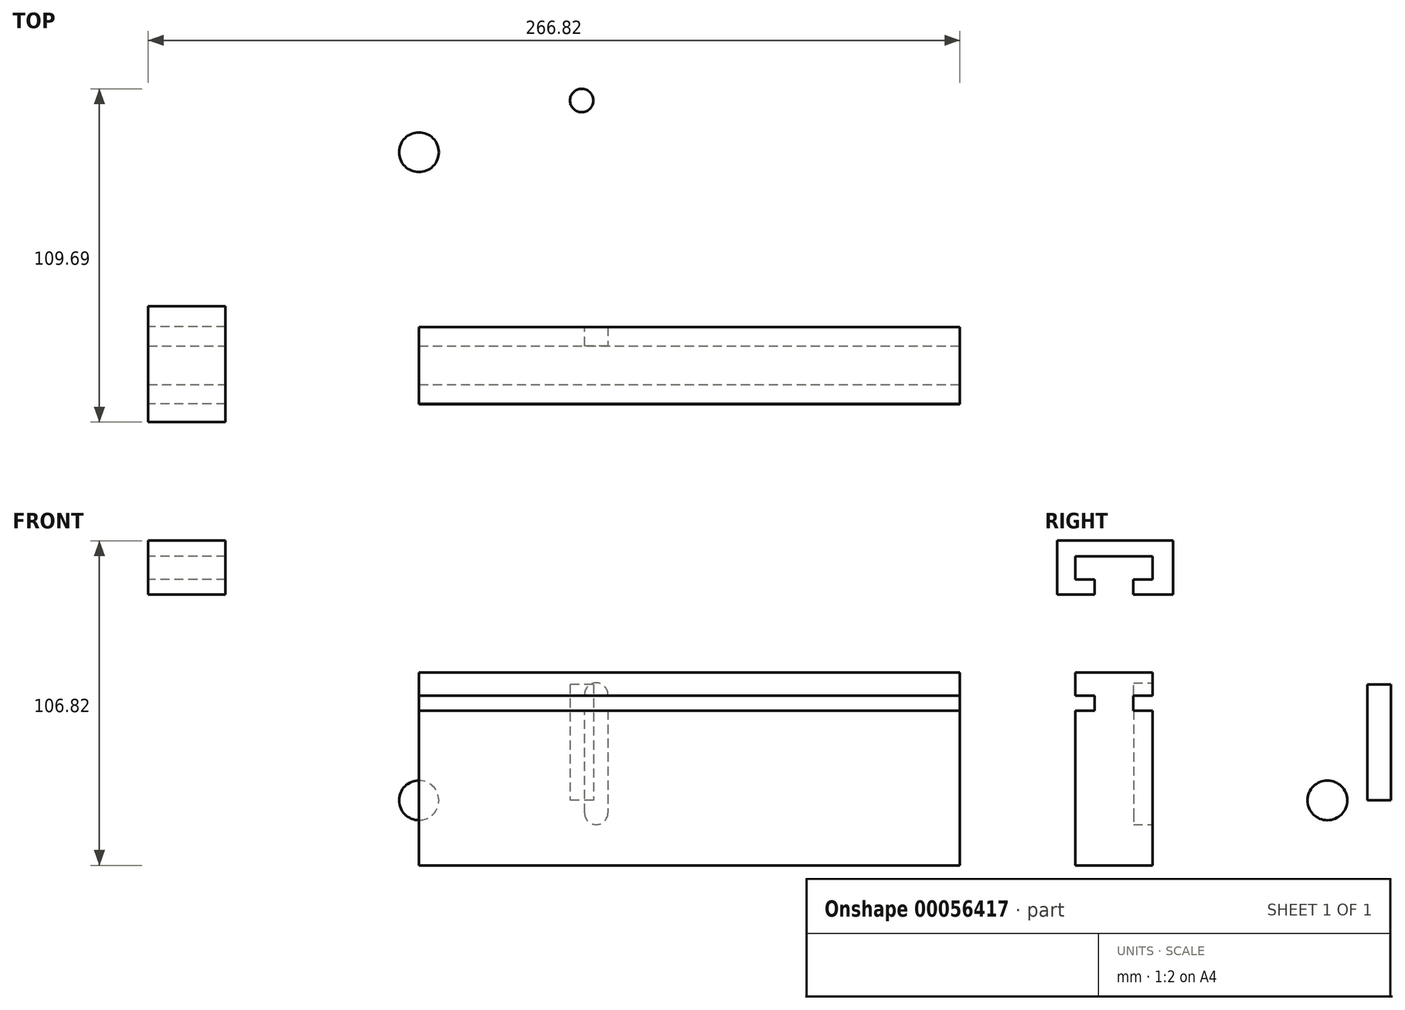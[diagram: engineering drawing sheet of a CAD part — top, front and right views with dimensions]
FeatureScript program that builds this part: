
annotation { "Feature Type Name" : "Feature", "Feature Type Description" : "" }
export const myFeature = defineFeature(function(context is Context, id is Id, definition is map)
    precondition{}
    {
        {
            var Q0;
            Q0=qCreatedBy(makeId("Right.planeOp"),FACE);
            var sketch = newSketch(context, id + "F0", { "sketchPlane" : qUnion([Q0])});
            skLineSegment(sketch, "E0.bottom", {"start": v(-46.62, 42.1) * mm, "end": v(-21.22, 42.1) * mm});
            skLineSegment(sketch, "E0.top", {"start": v(-46.62, -21.4) * mm, "end": v(-21.22, -21.4) * mm});
            skLineSegment(sketch, "E0.left", {"start": v(-46.62, 42.1) * mm, "end": v(-46.62, -21.4) * mm});
            skLineSegment(sketch, "E0.right", {"start": v(-21.22, 42.1) * mm, "end": v(-21.22, -21.4) * mm});
            skSolve(sketch);
        }
        {
            var Q0;
            Q0=makeQuery(id+"F0.imprint","IMPRINT",FACE,{"disambiguationData":[TD([[makeQuery(id+"F0.imprint","IMPRINT",EDGE,{"derivedFrom":sQuery(id+"F0.wireOp",EDGE,"E0.bottom")}),-1.0]])]});
            extrude(context, id + "F1", {"entities" : qUnion([Q0]), "depth" : 177.8 * mm});
        }
        {
            var Q0;
            Q0=qCreatedBy(makeId("Right.planeOp"),FACE);
            var sketch = newSketch(context, id + "F2", { "sketchPlane" : qUnion([Q0])});
            skLineSegment(sketch, "E1.rect.bottom", {"start": v(-52.7, 51.66) * mm, "end": v(-14.6, 51.66) * mm});
            skLineSegment(sketch, "E1.rect.top", {"start": v(-52.7, 33.88) * mm, "end": v(-14.6, 33.88) * mm});
            skLineSegment(sketch, "E1.rect.left", {"start": v(-52.7, 51.66) * mm, "end": v(-52.7, 33.88) * mm});
            skLineSegment(sketch, "E1.rect.right", {"start": v(-14.6, 51.66) * mm, "end": v(-14.6, 33.88) * mm});
            skPoint(sketch, "E1.rect.middle", {"position": v(-33.66, 42.77) * mm});
            skSolve(sketch);
        }
        {
            var Q0;
            Q0=qSketchRegion(id+"F2",true);
            extrude(context, id + "F3", {"entities" : qUnion([Q0]), "depth" : 25.4 * mm});
        }
        {
            var Q0;
            Q0=makeQuery(id+"F3.opExtrude","SWEPT_BODY",BODY,{"disambiguationData":[OSD([sQuery(id+"F2.wireOp",EDGE,"E1.rect.bottom"),sQuery(id+"F2.wireOp",EDGE,"E1.rect.top"),sQuery(id+"F2.wireOp",EDGE,"E1.rect.left"),sQuery(id+"F2.wireOp",EDGE,"E1.rect.right")])]});
            transform(context, id + "F4", {"entities" : qUnion([Q0]), "transformType" : TransformType.TRANSLATION_3D, "dx" : 0 * mm, "dy" : -51.7 * mm, "dz" : 1.05 * mm, "makeCopy" : false});
        }
        {
            var Q0;
            Q0=makeQuery(id+"F3.opExtrude","CAP_FACE",FACE,{"disambiguationData":[OSD([sQuery(id+"F2.wireOp",EDGE,"E1.rect.bottom"),sQuery(id+"F2.wireOp",EDGE,"E1.rect.top"),sQuery(id+"F2.wireOp",EDGE,"E1.rect.left"),sQuery(id+"F2.wireOp",EDGE,"E1.rect.right")])],"isStart":true});
            var sketch = newSketch(context, id + "F5", { "sketchPlane" : qUnion([Q0])});
            skLineSegment(sketch, "E2.bottom", {"start": v(73.03, 47.54) * mm, "end": v(98.43, 47.54) * mm});
            skLineSegment(sketch, "E2.top", {"start": v(73.03, 39.92) * mm, "end": v(98.43, 39.92) * mm});
            skLineSegment(sketch, "E2.left", {"start": v(73.03, 47.54) * mm, "end": v(73.03, 39.92) * mm});
            skLineSegment(sketch, "E2.right", {"start": v(98.43, 47.54) * mm, "end": v(98.43, 39.92) * mm});
            skSolve(sketch);
        }
        {
            var Q0;
            Q0=makeQuery(id+"F5.imprint","IMPRINT",FACE,{"disambiguationData":[TD([[makeQuery(id+"F5.imprint","IMPRINT",EDGE,{"derivedFrom":sQuery(id+"F5.wireOp",EDGE,"E2.bottom")}),-1.0]])]});
            extrude(context, id + "F6", {"entities" : qUnion([Q0]), "operationType" : NewBodyOperationType.REMOVE, "oppositeDirection" : true, "depth" : 41.28 * mm});
        }
        {
            var Q0;
            Q0=makeQuery(id+"F3.opExtrude","CAP_FACE",FACE,{"disambiguationData":[OSD([sQuery(id+"F2.wireOp",EDGE,"E1.rect.bottom"),sQuery(id+"F2.wireOp",EDGE,"E1.rect.top"),sQuery(id+"F2.wireOp",EDGE,"E1.rect.left"),sQuery(id+"F2.wireOp",EDGE,"E1.rect.right")])],"isStart":true});
            var sketch = newSketch(context, id + "F7", { "sketchPlane" : qUnion([Q0])});
            skLineSegment(sketch, "E3.bottom", {"start": v(73.03, 44.88) * mm, "end": v(85.73, 44.88) * mm});
            skLineSegment(sketch, "E3.top", {"start": v(73.03, 37.26) * mm, "end": v(85.73, 37.26) * mm});
            skLineSegment(sketch, "E3.left", {"start": v(73.03, 44.88) * mm, "end": v(73.03, 37.26) * mm});
            skLineSegment(sketch, "E3.right", {"start": v(85.73, 44.88) * mm, "end": v(85.73, 37.26) * mm});
            skSolve(sketch);
        }
        {
            var Q0;
            {var subQ0=sQuery(id+"F7.wireOp",EDGE,"E3.bottom");Q0=makeQuery(id+"F7.imprint","IMPRINT",FACE,{"disambiguationData":[TD([[makeQuery(id+"F7.imprint","IMPRINT",EDGE,{"derivedFrom":subQ0}),-1.0]])]});}
            var Q1;
            {var subQ0=sQuery(id+"F7.wireOp",EDGE,"E3.top");Q1=makeQuery(id+"F7.imprint","IMPRINT",FACE,{"disambiguationData":[TD([[makeQuery(id+"F7.imprint","IMPRINT",EDGE,{"derivedFrom":subQ0}),1.0]])]});}
            extrude(context, id + "F8", {"entities" : qUnion([Q0, Q1]), "depth" : 38.1 * mm});
        }
        {
            var Q0;
            Q0=makeQuery(id+"F8.opExtrude","SWEPT_BODY",BODY,{"disambiguationData":[OSD([sQuery(id+"F7.wireOp",EDGE,"E3.bottom"),sQuery(id+"F7.wireOp",EDGE,"E3.top"),sQuery(id+"F7.wireOp",EDGE,"E3.left"),sQuery(id+"F7.wireOp",EDGE,"E3.right")])]});
            transform(context, id + "F9", {"entities" : qUnion([Q0]), "transformType" : TransformType.TRANSLATION_3D, "dx" : 0 * mm, "dy" : -6.35 * mm, "dz" : -3.54 * mm, "makeCopy" : false});
        }
        {
            var Q0;
            Q0=makeQuery(id+"F8.opExtrude","SWEPT_BODY",BODY,{"disambiguationData":[OSD([sQuery(id+"F7.wireOp",EDGE,"E3.bottom"),sQuery(id+"F7.wireOp",EDGE,"E3.top"),sQuery(id+"F7.wireOp",EDGE,"E3.left"),sQuery(id+"F7.wireOp",EDGE,"E3.right")])]});
            transform(context, id + "F10", {"entities" : qUnion([Q0]), "transformType" : TransformType.TRANSLATION_3D, "dx" : 36.05 * mm, "dy" : 0 * mm, "dz" : 0 * mm, "makeCopy" : false});
        }
        {
            var Q0;
            Q0=makeQuery(id+"F8.opExtrude","SWEPT_BODY",BODY,{"disambiguationData":[OSD([sQuery(id+"F7.wireOp",EDGE,"E3.bottom"),sQuery(id+"F7.wireOp",EDGE,"E3.top"),sQuery(id+"F7.wireOp",EDGE,"E3.left"),sQuery(id+"F7.wireOp",EDGE,"E3.right")])]});
            var Q1;
            Q1=makeQuery(id+"F3.opExtrude","SWEPT_BODY",BODY,{"disambiguationData":[OSD([sQuery(id+"F2.wireOp",EDGE,"E1.rect.bottom"),sQuery(id+"F2.wireOp",EDGE,"E1.rect.top"),sQuery(id+"F2.wireOp",EDGE,"E1.rect.left"),sQuery(id+"F2.wireOp",EDGE,"E1.rect.right")])]});
            booleanBodies(context, id + "F11", {"operationType" : BooleanOperationType.SUBTRACTION, "tools" : qUnion([Q0]), "targets" : qUnion([Q1])});
        }
        {
            var Q0;
            Q0=makeQuery(id+"F3.opExtrude","SWEPT_BODY",BODY,{"disambiguationData":[OSD([sQuery(id+"F2.wireOp",EDGE,"E1.rect.bottom"),sQuery(id+"F2.wireOp",EDGE,"E1.rect.top"),sQuery(id+"F2.wireOp",EDGE,"E1.rect.left"),sQuery(id+"F2.wireOp",EDGE,"E1.rect.right")])]});
            transform(context, id + "F12", {"entities" : qUnion([Q0]), "transformType" : TransformType.TRANSLATION_3D, "dx" : 0 * mm, "dy" : 51.86 * mm, "dz" : -5.42 * mm, "makeCopy" : false});
        }
        {
            var Q0;
            Q0=makeQuery(id+"F3.opExtrude","SWEPT_BODY",BODY,{"disambiguationData":[OSD([sQuery(id+"F2.wireOp",EDGE,"E1.rect.bottom"),sQuery(id+"F2.wireOp",EDGE,"E1.rect.top"),sQuery(id+"F2.wireOp",EDGE,"E1.rect.left"),sQuery(id+"F2.wireOp",EDGE,"E1.rect.right")])]});
            transform(context, id + "F13", {"entities" : qUnion([Q0]), "transformType" : TransformType.TRANSLATION_3D, "dx" : 177.8 * mm, "dy" : 0 * mm, "dz" : 0 * mm, "makeCopy" : true});
        }
        {
            var Q0;
            Q0=makeQuery(id+"F3.opExtrude","SWEPT_BODY",BODY,{"disambiguationData":[OSD([sQuery(id+"F2.wireOp",EDGE,"E1.rect.bottom"),sQuery(id+"F2.wireOp",EDGE,"E1.rect.top"),sQuery(id+"F2.wireOp",EDGE,"E1.rect.left"),sQuery(id+"F2.wireOp",EDGE,"E1.rect.right")])]});
            var Q1;
            Q1=makeQuery(id+"F1.opExtrude","CAP_EDGE",EDGE,{"disambiguationData":[OSD([sQuery(id+"F0.wireOp",EDGE,"E0.left")])],"isStart":true});
            transform(context, id + "F14", {"entities" : qUnion([Q0]), "transformType" : TransformType.TRANSLATION_3D, "dx" : -89.02 * mm, "dy" : 0 * mm, "dz" : 38.15 * mm, "makeCopy" : false});
        }
        {
            var Q0;
            Q0=makeQuery(id+"F13.opPattern","COPY",BODY,{"derivedFrom":makeQuery(id+"F3.opExtrude","SWEPT_BODY",BODY,{"disambiguationData":[OSD([sQuery(id+"F2.wireOp",EDGE,"E1.rect.bottom"),sQuery(id+"F2.wireOp",EDGE,"E1.rect.top"),sQuery(id+"F2.wireOp",EDGE,"E1.rect.left"),sQuery(id+"F2.wireOp",EDGE,"E1.rect.right")])]}),"instanceName":"1"});
            transform(context, id + "F15", {"entities" : qUnion([Q0]), "transformType" : TransformType.TRANSLATION_3D, "dx" : 9.13 * mm, "dy" : 0 * mm, "dz" : 0 * mm, "makeCopy" : false});
        }
        {
            var Q0;
            Q0=makeQuery(id+"F13.opPattern","COPY",FACE,{"derivedFrom":makeQuery(id+"F3.opExtrude","CAP_FACE",FACE,{"disambiguationData":[OSD([sQuery(id+"F2.wireOp",EDGE,"E1.rect.bottom"),sQuery(id+"F2.wireOp",EDGE,"E1.rect.top"),sQuery(id+"F2.wireOp",EDGE,"E1.rect.left"),sQuery(id+"F2.wireOp",EDGE,"E1.rect.right")])],"isStart":true}),"instanceName":"1"});
            extrude(context, id + "F16", {"entities" : qUnion([Q0]), "depth" : 231.78 * mm});
        }
        {
            var Q0;
            Q0=makeQuery(id+"F13.opPattern","COPY",BODY,{"derivedFrom":makeQuery(id+"F3.opExtrude","SWEPT_BODY",BODY,{"disambiguationData":[OSD([sQuery(id+"F2.wireOp",EDGE,"E1.rect.bottom"),sQuery(id+"F2.wireOp",EDGE,"E1.rect.top"),sQuery(id+"F2.wireOp",EDGE,"E1.rect.left"),sQuery(id+"F2.wireOp",EDGE,"E1.rect.right")])]}),"instanceName":"1"});
            var Q1;
            Q1=makeQuery(id+"F1.opExtrude","SWEPT_BODY",BODY,{"disambiguationData":[OSD([sQuery(id+"F0.wireOp",EDGE,"E0.bottom"),sQuery(id+"F0.wireOp",EDGE,"E0.top"),sQuery(id+"F0.wireOp",EDGE,"E0.left"),sQuery(id+"F0.wireOp",EDGE,"E0.right")])]});
            booleanBodies(context, id + "F17", {"operationType" : BooleanOperationType.SUBTRACTION, "tools" : qUnion([Q0]), "targets" : qUnion([Q1])});
        }
        {
            var Q0;
            Q0=makeQuery(id+"F16.opExtrude","SWEPT_BODY",BODY,{"disambiguationData":[OSD([sQuery(id+"F2.wireOp",EDGE,"E1.rect.bottom"),sQuery(id+"F2.wireOp",EDGE,"E1.rect.top"),sQuery(id+"F2.wireOp",EDGE,"E1.rect.left"),sQuery(id+"F2.wireOp",EDGE,"E1.rect.right")])]});
            var Q1;
            Q1=makeQuery(id+"F1.opExtrude","SWEPT_BODY",BODY,{"disambiguationData":[OSD([sQuery(id+"F0.wireOp",EDGE,"E0.bottom"),sQuery(id+"F0.wireOp",EDGE,"E0.top"),sQuery(id+"F0.wireOp",EDGE,"E0.left"),sQuery(id+"F0.wireOp",EDGE,"E0.right")])]});
            booleanBodies(context, id + "F18", {"operationType" : BooleanOperationType.SUBTRACTION, "tools" : qUnion([Q0]), "targets" : qUnion([Q1])});
        }
        {
            var Q0;
            Q0=qCreatedBy(makeId("Front.planeOp"),FACE);
            var sketch = newSketch(context, id + "F19", { "sketchPlane" : qUnion([Q0])});
            skArc(sketch, "E4", {"start": v(62.11, 34.83) * mm, "mid": v(58.26, 38.67) * mm, "end": v(54.41, 34.83) * mm});
            skArc(sketch, "E5", {"start": v(54.41, -4.13) * mm, "mid": v(58.26, -7.98) * mm, "end": v(62.11, -4.13) * mm});
            skLineSegment(sketch, "E6", {"start": v(62.11, 34.83) * mm, "end": v(62.11, -4.13) * mm});
            skLineSegment(sketch, "E7", {"start": v(54.41, -4.13) * mm, "end": v(54.41, 34.83) * mm});
            skSolve(sketch);
        }
        {
            var Q0;
            {var subQ0=sQuery(id+"F19.wireOp",EDGE,"E4");Q0=makeQuery(id+"F19.imprint","IMPRINT",FACE,{"disambiguationData":[TD([[makeQuery(id+"F19.imprint","IMPRINT",EDGE,{"derivedFrom":subQ0}),1.0]])]});}
            extrude(context, id + "F20", {"entities" : qUnion([Q0]), "operationType" : NewBodyOperationType.REMOVE, "depth" : 27.43 * mm});
        }
        {
            var Q0;
            Q0=qCreatedBy(makeId("Top.planeOp"),FACE);
            var sketch = newSketch(context, id + "F21", { "sketchPlane" : qUnion([Q0])});
            skCircle(sketch, "E8", {"center": v(53.5, 53.29) * mm, "radius": 3.85 * mm});
            skSolve(sketch);
        }
        {
            var Q0;
            Q0=makeQuery(id+"F21.imprint","IMPRINT",FACE,{"disambiguationData":[TD([[makeQuery(id+"F21.imprint","IMPRINT",EDGE,{"derivedFrom":sQuery(id+"F21.wireOp",EDGE,"E8")}),1.0]])]});
            extrude(context, id + "F22", {"entities" : qUnion([Q0]), "depth" : 38.1 * mm});
        }
        {
            var Q0;
            Q0=qCreatedBy(makeId("Right.planeOp"),FACE);
            var sketch = newSketch(context, id + "F23", { "sketchPlane" : qUnion([Q0])});
            skArc(sketch, "E9", {"start": v(29.74, 0) * mm, "mid": v(36.27, -6.53) * mm, "end": v(42.8, 0) * mm});
            skLineSegment(sketch, "E10", {"start": v(42.8, 0) * mm, "end": v(29.74, 0) * mm});
            skSolve(sketch);
        }
        {
            var Q0;
            Q0=makeQuery(id+"F23.imprint","IMPRINT",FACE,{"disambiguationData":[TD([[makeQuery(id+"F23.imprint","IMPRINT",EDGE,{"derivedFrom":sQuery(id+"F23.wireOp",EDGE,"E9")}),1.0]])]});
            var Q1;
            Q1=sQuery(id+"F23.wireOp",EDGE,"E10");
            revolve(context, id + "F24", {"entities" : qUnion([Q0]), "axis" : qUnion([Q1]), "revolveType" : RevolveType.FULL});
        }
    });
